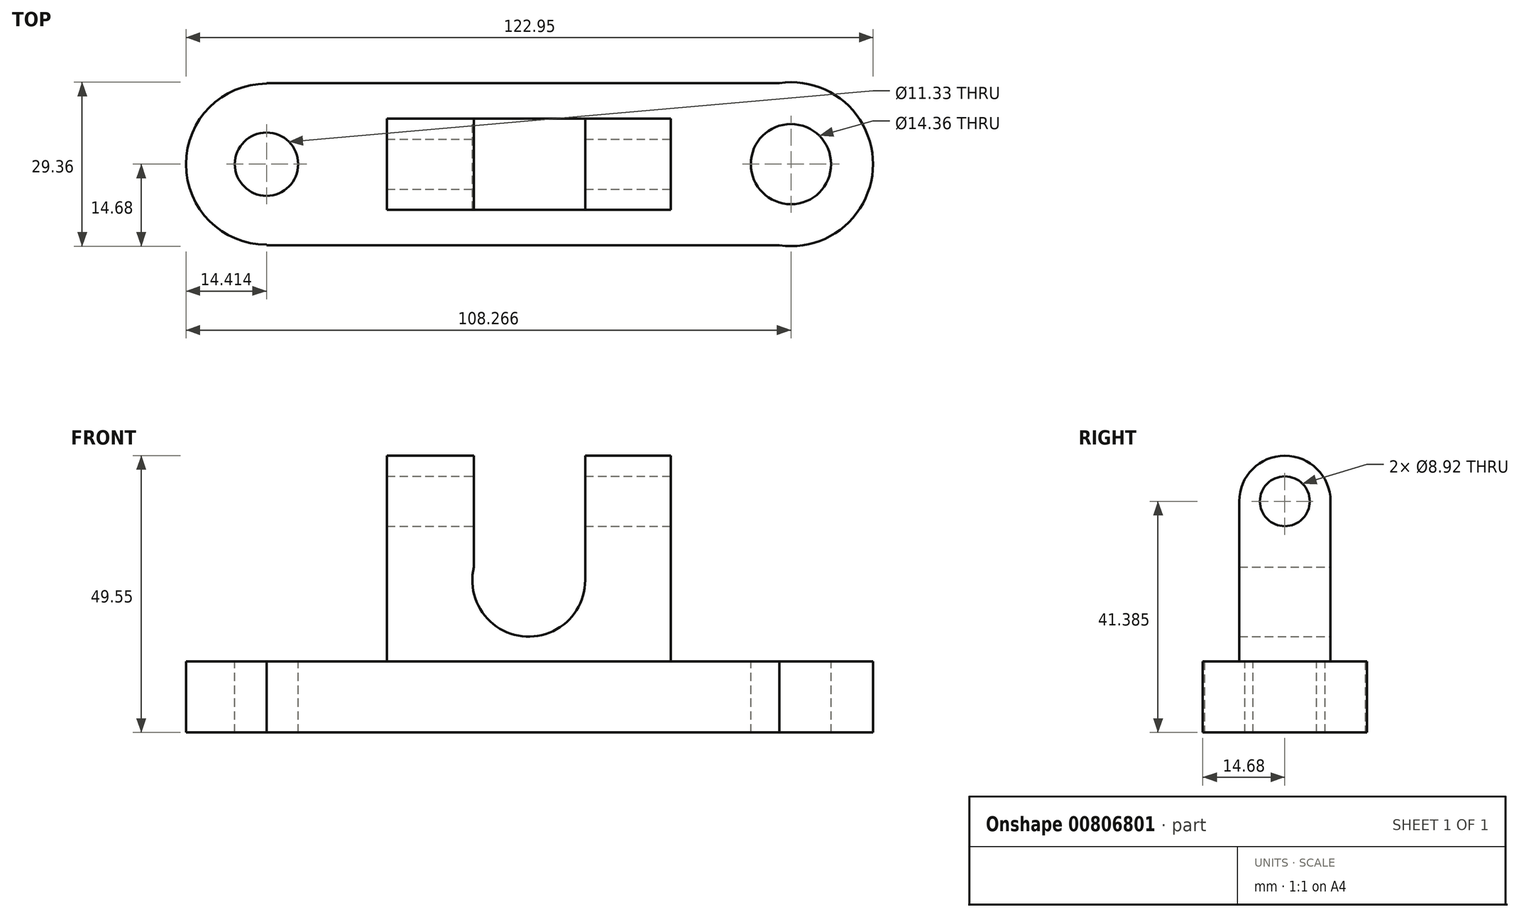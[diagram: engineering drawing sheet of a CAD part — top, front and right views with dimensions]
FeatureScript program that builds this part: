
annotation { "Feature Type Name" : "Feature", "Feature Type Description" : "" }
export const myFeature = defineFeature(function(context is Context, id is Id, definition is map)
    precondition{}
    {
        {
            var Q0;
            Q0=qCreatedBy(makeId("Top.planeOp"),FACE);
            var sketch = newSketch(context, id + "F0", { "sketchPlane" : qUnion([Q0])});
            skLineSegment(sketch, "E0.bottom", {"start": v(46.93, 14.53) * mm, "end": v(-46.93, 14.53) * mm});
            skLineSegment(sketch, "E0.top", {"start": v(46.93, -14.53) * mm, "end": v(-46.93, -14.53) * mm});
            skLineSegment(sketch, "E0.right", {"start": v(-46.93, 14.53) * mm, "end": v(-46.93, 14.41) * mm});
            skPoint(sketch, "E0.middle", {"position": v(0, 0) * mm});
            skArc(sketch, "E1", {"start": v(44.84, -14.53) * mm, "mid": v(61.6, 0) * mm, "end": v(44.84, 14.53) * mm});
            skArc(sketch, "E2", {"start": v(-46.93, 14.41) * mm, "mid": v(-61.34, 0) * mm, "end": v(-46.93, -14.41) * mm});
            skLineSegment(sketch, "E3.trimOffspring", {"start": v(-46.93, -14.41) * mm, "end": v(-46.93, -14.53) * mm});
            skSolve(sketch);
        }
        {
            var Q0;
            {var subQ1=sQuery(id+"F0.wireOp",EDGE,"E0.right");Q0=makeQuery(id+"F0.imprint","IMPRINT",FACE,{"disambiguationData":[TD([[makeQuery(id+"F0.imprint","IMPRINT",EDGE,{"derivedFrom":subQ1}),1.0]])]});}
            extrude(context, id + "F1", {"entities" : qUnion([Q0]), "depth" : 12.7 * mm, "offsetDistance" : 25.4 * mm});
        }
        {
            var Q0;
            Q0=makeQuery(id+"F1.opExtrude","CAP_FACE",FACE,{"disambiguationData":[OSD([sQuery(id+"F0.wireOp",EDGE,"E0.bottom"),sQuery(id+"F0.wireOp",EDGE,"E0.top"),sQuery(id+"F0.wireOp",EDGE,"E0.right"),sQuery(id+"F0.wireOp",EDGE,"E1"),sQuery(id+"F0.wireOp",EDGE,"E2"),sQuery(id+"F0.wireOp",EDGE,"E3.trimOffspring")])],"isStart":false});
            var sketch = newSketch(context, id + "F2", { "sketchPlane" : qUnion([Q0])});
            skCircle(sketch, "E4", {"center": v(-46.93, 0) * mm, "radius": 5.67 * mm});
            skCircle(sketch, "E5", {"center": v(46.93, 0) * mm, "radius": 7.18 * mm});
            skSolve(sketch);
        }
        {
            var Q0;
            Q0=makeQuery(id+"F2.imprint","IMPRINT",FACE,{"disambiguationData":[TD([[makeQuery(id+"F2.imprint","IMPRINT",EDGE,{"derivedFrom":sQuery(id+"F2.wireOp",EDGE,"E5")}),1.0]])]});
            var Q1;
            Q1=makeQuery(id+"F2.imprint","IMPRINT",FACE,{"disambiguationData":[TD([[makeQuery(id+"F2.imprint","IMPRINT",EDGE,{"derivedFrom":sQuery(id+"F2.wireOp",EDGE,"E4")}),1.0]])]});
            extrude(context, id + "F3", {"entities" : qUnion([Q0, Q1]), "operationType" : NewBodyOperationType.REMOVE, "oppositeDirection" : true, "depth" : 25.4 * mm, "offsetDistance" : 25.4 * mm});
        }
        {
            var Q0;
            Q0=qCreatedBy(makeId("Right.planeOp"),FACE);
            var sketch = newSketch(context, id + "F4", { "sketchPlane" : qUnion([Q0])});
            skLineSegment(sketch, "E6.bottom", {"start": v(8.17, 12.6) * mm, "end": v(-8.17, 12.6) * mm});
            skLineSegment(sketch, "E6.left", {"start": v(8.17, 12.6) * mm, "end": v(8.17, 41.38) * mm});
            skLineSegment(sketch, "E6.right", {"start": v(-8.17, 12.6) * mm, "end": v(-8.17, 41.38) * mm});
            skPoint(sketch, "E6.middle", {"position": v(0, 26.99) * mm});
            skArc(sketch, "E7", {"start": v(8.17, 41.38) * mm, "mid": v(0, 49.55) * mm, "end": v(-8.17, 41.38) * mm});
            skSolve(sketch);
        }
        {
            var Q0;
            Q0=makeQuery(id+"F4.imprint","IMPRINT",FACE,{"disambiguationData":[TD([[makeQuery(id+"F4.imprint","IMPRINT",EDGE,{"derivedFrom":sQuery(id+"F4.wireOp",EDGE,"E6.bottom")}),-1.0]])]});
            extrude(context, id + "F5", {"entities" : qUnion([Q0]), "operationType" : NewBodyOperationType.ADD, "endBound" : BoundingType.SYMMETRIC, "depth" : 50.8 * mm, "offsetDistance" : 25.4 * mm});
        }
        {
            var Q0;
            Q0=makeQuery(id+"F5.opExtrude","CAP_FACE",FACE,{"disambiguationData":[OSD([sQuery(id+"F4.wireOp",EDGE,"E6.bottom"),sQuery(id+"F4.wireOp",EDGE,"E6.left"),sQuery(id+"F4.wireOp",EDGE,"E6.right"),sQuery(id+"F4.wireOp",EDGE,"E7")])],"isStart":false});
            var sketch = newSketch(context, id + "F6", { "sketchPlane" : qUnion([Q0])});
            skCircle(sketch, "E8", {"center": v(0, 41.38) * mm, "radius": 4.46 * mm});
            skSolve(sketch);
        }
        {
            var Q0;
            Q0=makeQuery(id+"F6.imprint","IMPRINT",FACE,{"disambiguationData":[TD([[makeQuery(id+"F6.imprint","IMPRINT",EDGE,{"derivedFrom":sQuery(id+"F6.wireOp",EDGE,"E8")}),1.0]])]});
            extrude(context, id + "F7", {"entities" : qUnion([Q0]), "operationType" : NewBodyOperationType.REMOVE, "endBound" : BoundingType.SYMMETRIC, "oppositeDirection" : true, "depth" : 127 * mm, "offsetDistance" : 25.4 * mm});
        }
        {
            var Q0;
            Q0=qCreatedBy(makeId("Front.planeOp"),FACE);
            var sketch = newSketch(context, id + "F8", { "sketchPlane" : qUnion([Q0])});
            skLineSegment(sketch, "E9.bottom", {"start": v(-9.83, 50.24) * mm, "end": v(10.1, 50.24) * mm});
            skLineSegment(sketch, "E9.left", {"start": v(-9.83, 50.24) * mm, "end": v(-9.83, 27.27) * mm});
            skLineSegment(sketch, "E9.right", {"start": v(10.1, 50.24) * mm, "end": v(10.1, 27.27) * mm});
            skArc(sketch, "E10", {"start": v(-9.83, 29.61) * mm, "mid": v(-1.18, 17.23) * mm, "end": v(10.1, 27.27) * mm});
            skSolve(sketch);
        }
        {
            var Q0;
            {var subQ0=sQuery(id+"F8.wireOp",EDGE,"E9.bottom");Q0=makeQuery(id+"F8.imprint","IMPRINT",FACE,{"disambiguationData":[TD([[makeQuery(id+"F8.imprint","IMPRINT",EDGE,{"derivedFrom":subQ0}),-1.0]])]});}
            extrude(context, id + "F9", {"entities" : qUnion([Q0]), "operationType" : NewBodyOperationType.REMOVE, "endBound" : BoundingType.SYMMETRIC, "depth" : 76.2 * mm, "offsetDistance" : 25.4 * mm});
        }
    });
